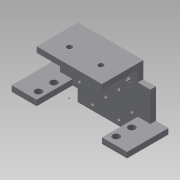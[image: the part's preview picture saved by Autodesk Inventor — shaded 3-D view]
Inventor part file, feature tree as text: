
AUTODESK INVENTOR PART (.ipt)
format: ipt  version: 2015 SP1 (Build 190203100, 203)  size: 516,608 bytes
history: native  units: mm
features: sketch x23, extrude x22, reference x13, projected_geometry x7, mirror x5
ambient origin geometry x8: Origin, YZ Plane, XZ Plane, XY Plane, X Axis, Y Axis, Z Axis, Center Point
bodies: Solid1 (feature_tree)
feature tree (70):
  extrude  "Extrusion1"  Depth=29.21mm
  extrude  "Extrusion2"  Depth=3.5mm
  extrude  "Extrusion3"  Depth=57.15mm TaperAngle=0.0deg
  sketch  "Sketch5"  dims[d8=57.15mm d9=0.0mm d11=25.147mm d12=0.0mm]
  extrude  "Extrusion4"  Depth=25.147mm TaperAngle=0.0deg
  extrude  "Extrusion5"  Depth=21.1822mm
  mirror  "Mirror1"
  extrude  "Extrusion6"  Depth=25.147mm TaperAngle=0.0deg
  extrude  "Extrusion8"  Depth=3.5mm TaperAngle=0.0deg
  extrude  "Extrusion9"  Depth=3.5mm
  extrude  "Extrusion10"  Depth=7.95mm TaperAngle=0.0deg
  sketch  "Sketch16"  dims[d38=7.95mm d39=0.0mm d43=7.95mm d44=0.0mm]
  extrude  "Extrusion11"  Depth=7.95mm TaperAngle=0.0deg
  sketch  "Sketch19"  dims[d47=3.5mm d48=0.0mm d50=2.0mm]
  extrude  "Extrusion12"  Depth=2.0mm
  mirror  "Mirror2"
  extrude  "Extrusion13"  Depth=3.5mm TaperAngle=0.0deg
  extrude  "Extrusion15"  Depth=7.95mm TaperAngle=0.0deg
  sketch  "Sketch24"  dims[d59=3.5mm d60=0.0mm d61=3.5mm d62=0.0mm]
  extrude  "Extrusion17"  Depth=3.5mm TaperAngle=0.0deg
  extrude  "Extrusion18"  Depth=3.5mm TaperAngle=0.0deg
  mirror  "Mirror4"
  extrude  "Extrusion19"  [1 undecoded]
  extrude  "Extrusion20"  [1 undecoded]
  sketch  "Sketch29"
  sketch  "Sketch30"
  extrude  "Extrusion21"  [1 undecoded]
  mirror  "Mirror5"
  extrude  "Extrusion22"  [1 undecoded]
  extrude  "Extrusion23"  [1 undecoded]
  extrude  "Extrusion24"  [1 undecoded]
  mirror  "Mirror6"
  extrude  "Extrusion25"  [1 undecoded]
  sketch  "Sketch1"  dims[d0=57.15mm d1=29.21mm]
  sketch  "Sketch2"  dims[d2=3.5mm d3=0.0mm d4=3.5mm]
  sketch  "Sketch4"  dims[d5=3.5mm d6=57.15mm d7=0.0mm]
  sketch  "Sketch9"  dims[d15=25.147mm d16=0.0mm d18=21.1822mm]
  reference  "Reference3"
  reference  "Reference4"
  sketch  "Sketch11"  dims[d19=22.428mm d20=25.147mm d21=0.0mm]
  reference  "Reference7"
  sketch  "Sketch13"  dims[d24=3.5mm d25=0.0mm d26=3.5mm d27=0.0mm]
  sketch  "Sketch14"  dims[d28=3.5mm d29=0.0mm d30=3.5mm]
  sketch  "Sketch15"  dims[d33=22.682mm d34=0.0mm d36=7.95mm d37=0.0mm]
  reference  "Reference24"
  projected_geometry  "Projected Loop1"
  sketch  "Sketch21"  dims[d51=3.5mm d52=0.0mm d53=3.5mm d54=0.0mm]
  projected_geometry  "Projected Loop2"
  sketch  "Sketch23"  dims[d55=3.5mm d56=0.0mm d57=7.95mm d58=0.0mm]
  reference  "Reference26"
  reference  "Reference27"
  reference  "Reference28"
  reference  "Reference29"
  reference  "Reference30"
  sketch  "Sketch26"  dims[d63=3.5mm d64=0.0mm d65=3.5mm d66=0.0mm]
  sketch  "Sketch27"  dims[d67=3.9751mm]
  sketch  "Sketch28"
  projected_geometry  "Projected Loop3"
  projected_geometry  "Projected Loop4"
  projected_geometry  "Projected Loop5"
  projected_geometry  "Projected Loop6"
  projected_geometry  "Projected Loop7"
  sketch  "Sketch31"
  sketch  "Sketch32"
  reference  "Reference33"
  reference  "Reference34"
  reference  "Reference35"
  reference  "Reference36"
  sketch  "Sketch33"
  sketch  "Sketch34"
note: 7 required parameter values undecoded (feature->parameter linkage not recoverable at this tier; creation-order binding heuristic only, values carry confidence <= 0.55)
